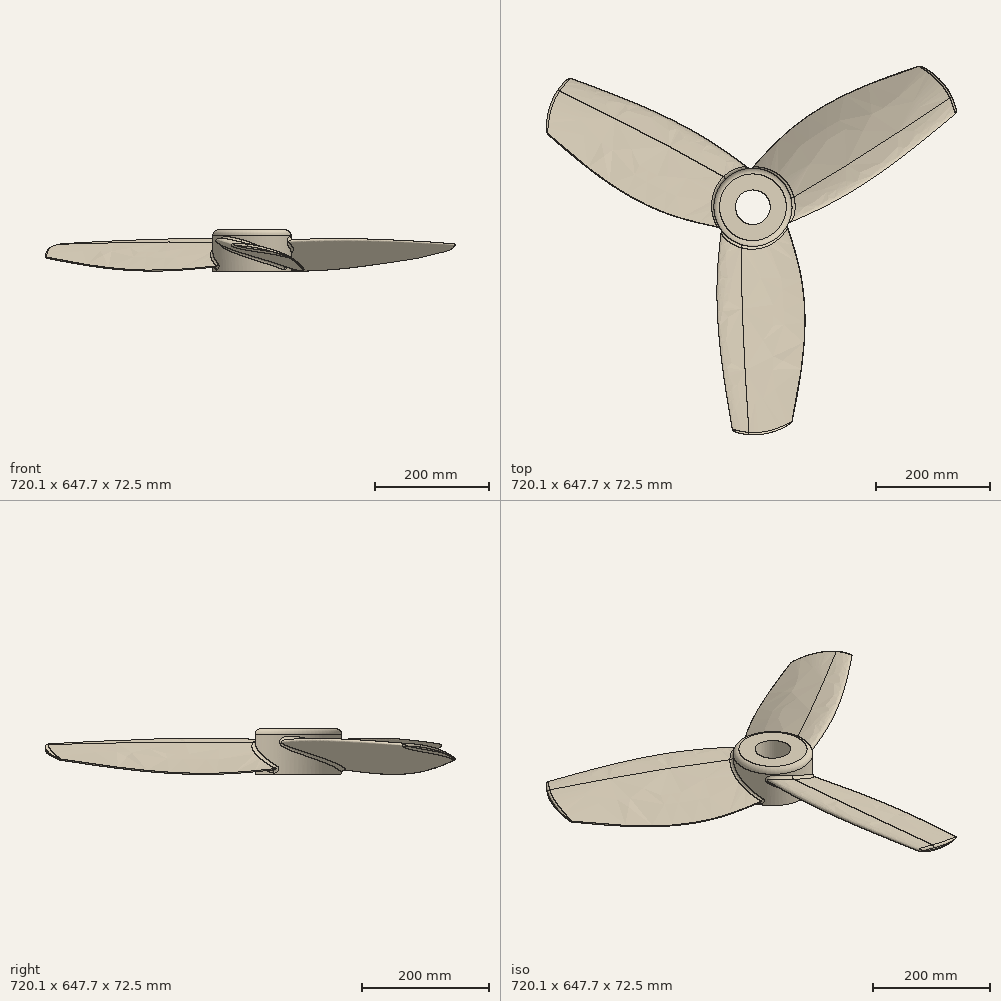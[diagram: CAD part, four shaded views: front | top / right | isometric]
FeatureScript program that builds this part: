
annotation { "Feature Type Name" : "Feature", "Feature Type Description" : "" }
export const myFeature = defineFeature(function(context is Context, id is Id, definition is map)
    precondition{}
    {
        {
            var Q0;
            Q0=qCreatedBy(makeId("Front.planeOp"),FACE);
            var sketch = newSketch(context, id + "F0", { "sketchPlane" : qUnion([Q0])});
            skLineSegment(sketch, "E0", {"start": v(-25.68, 10.16) * mm, "end": v(0, 0) * mm, "construction": true});
            skLineSegment(sketch, "E1", {"start": v(0, 0) * mm, "end": v(25.68, -10.16) * mm, "construction": true});
            skLineSegment(sketch, "E2", {"start": v(25.68, -10.16) * mm, "end": v(51.36, -20.31) * mm, "construction": true});
            skLineSegment(sketch, "E3", {"start": v(51.36, -20.31) * mm, "end": v(77.03, -30.47) * mm, "construction": true});
            skLineSegment(sketch, "E4", {"start": v(0, 0) * mm, "end": v(3.73, 9.44) * mm, "construction": true});
            skLineSegment(sketch, "E5", {"start": v(-25.68, 10.16) * mm, "end": v(-23.81, 14.88) * mm, "construction": true});
            skFitSpline(sketch, "E6", {"points": [v(-25.68, 10.16) * mm, v(3.73, 9.44) * mm, v(77.03, -30.47) * mm], "startDerivative": vector(15.03, 38) * mm, "endDerivative": vector(104.92, -93.69) * mm});
            skPoint(sketch, "E7", {"position": v(1.87, 4.72) * mm});
            skLineSegment(sketch, "E8", {"start": v(-23.81, 14.88) * mm, "end": v(1.87, 4.72) * mm, "construction": true});
            skLineSegment(sketch, "E9", {"start": v(0, 0) * mm, "end": v(-1.87, -4.72) * mm, "construction": true});
            skLineSegment(sketch, "E10", {"start": v(-25.68, 10.16) * mm, "end": v(-27.54, 5.44) * mm, "construction": true});
            skFitSpline(sketch, "E11", {"points": [v(-25.68, 10.16) * mm, v(-1.87, -4.72) * mm, v(77.03, -30.47) * mm], "startDerivative": vector(-15.23, -38.5) * mm, "endDerivative": vector(121.84, -48.19) * mm});
            skLineSegment(sketch, "E12", {"start": v(51.36, -20.31) * mm, "end": v(55.09, -10.87) * mm, "construction": true});
            skSolve(sketch);
        }
        {
            var Q0;
            Q0=qCreatedBy(makeId("Front.planeOp"),FACE);
            cPlane(context, id + "F1", {"entities" : qUnion([Q0]), "cplaneType" : CPlaneType.OFFSET, "offset" : 125 * mm, "width" : 150 * mm, "height" : 150 * mm});
        }
        {
            var Q0;
            Q0=qCreatedBy(id+"F1.planeOp",FACE);
            var sketch = newSketch(context, id + "F2", { "sketchPlane" : qUnion([Q0])});
            skLineSegment(sketch, "E13", {"start": v(-38.33, 14.06) * mm, "end": v(0, 0) * mm, "construction": true});
            skLineSegment(sketch, "E14", {"start": v(0, 0) * mm, "end": v(38.33, -14.06) * mm, "construction": true});
            skLineSegment(sketch, "E15", {"start": v(38.33, -14.06) * mm, "end": v(76.67, -28.12) * mm, "construction": true});
            skLineSegment(sketch, "E16", {"start": v(76.67, -28.12) * mm, "end": v(115, -42.17) * mm, "construction": true});
            skLineSegment(sketch, "E17", {"start": v(0, 0) * mm, "end": v(4.06, 11.06) * mm, "construction": true});
            skLineSegment(sketch, "E18", {"start": v(-38.33, 14.06) * mm, "end": v(-36.3, 19.59) * mm, "construction": true});
            skFitSpline(sketch, "E19", {"points": [v(-38.33, 14.06) * mm, v(4.06, 11.06) * mm, v(115, -42.17) * mm], "startDerivative": vector(16.44, 44.82) * mm, "endDerivative": vector(163.27, -119.63) * mm});
            skPoint(sketch, "E20", {"position": v(2.03, 5.53) * mm});
            skLineSegment(sketch, "E21", {"start": v(-36.3, 19.59) * mm, "end": v(2.03, 5.53) * mm, "construction": true});
            skLineSegment(sketch, "E22", {"start": v(0, 0) * mm, "end": v(-2.03, -5.53) * mm, "construction": true});
            skLineSegment(sketch, "E23", {"start": v(-38.33, 14.06) * mm, "end": v(-40.36, 8.53) * mm, "construction": true});
            skFitSpline(sketch, "E24", {"points": [v(-38.33, 14.06) * mm, v(-2.03, -5.53) * mm, v(115, -42.17) * mm], "startDerivative": vector(-16.57, -45.19) * mm, "endDerivative": vector(181.7, -66.64) * mm});
            skLineSegment(sketch, "E25", {"start": v(76.67, -28.12) * mm, "end": v(80.72, -17.06) * mm, "construction": true});
            skSolve(sketch);
        }
        {
            var Q0;
            Q0=qCreatedBy(makeId("Front.planeOp"),FACE);
            cPlane(context, id + "F3", {"entities" : qUnion([Q0]), "cplaneType" : CPlaneType.OFFSET, "offset" : 400 * mm, "width" : 150 * mm, "height" : 150 * mm});
        }
        {
            var Q0;
            Q0=qCreatedBy(id+"F3.planeOp",FACE);
            var sketch = newSketch(context, id + "F4", { "sketchPlane" : qUnion([Q0])});
            skLineSegment(sketch, "E26", {"start": v(-10.03, 5.14) * mm, "end": v(16.27, 0) * mm, "construction": true});
            skLineSegment(sketch, "E27", {"start": v(16.27, 0) * mm, "end": v(42.56, -5.14) * mm, "construction": true});
            skLineSegment(sketch, "E28", {"start": v(42.56, -5.14) * mm, "end": v(68.86, -10.28) * mm, "construction": true});
            skLineSegment(sketch, "E29", {"start": v(68.86, -10.28) * mm, "end": v(95.16, -15.42) * mm, "construction": true});
            skLineSegment(sketch, "E30", {"start": v(16.27, 0) * mm, "end": v(17.61, 6.9) * mm, "construction": true});
            skLineSegment(sketch, "E31", {"start": v(-10.03, 5.14) * mm, "end": v(-9.36, 8.59) * mm, "construction": true});
            skFitSpline(sketch, "E32", {"points": [v(-10.03, 5.14) * mm, v(17.61, 6.9) * mm, v(95.16, -15.42) * mm], "startDerivative": vector(5.47, 28.01) * mm, "endDerivative": vector(118.7, -57.28) * mm});
            skPoint(sketch, "E33", {"position": v(16.94, 3.45) * mm});
            skLineSegment(sketch, "E34", {"start": v(-9.36, 8.59) * mm, "end": v(16.94, 3.45) * mm, "construction": true});
            skLineSegment(sketch, "E35", {"start": v(16.27, 0) * mm, "end": v(15.6, -3.45) * mm, "construction": true});
            skLineSegment(sketch, "E36", {"start": v(-10.03, 5.14) * mm, "end": v(-10.7, 1.7) * mm, "construction": true});
            skFitSpline(sketch, "E37", {"points": [v(-10.03, 5.14) * mm, v(15.6, -3.45) * mm, v(95.16, -15.42) * mm], "startDerivative": vector(-5.51, -28.2) * mm, "endDerivative": vector(124.61, -24.36) * mm});
            skLineSegment(sketch, "E38", {"start": v(68.86, -10.28) * mm, "end": v(70.2, -3.38) * mm, "construction": true});
            skSolve(sketch);
        }
        {
            var Q0;
            Q0=qSketchRegion(id+"F0",true);
            var Q1;
            Q1=qSketchRegion(id+"F2",true);
            var Q2;
            Q2=qSketchRegion(id+"F4",true);
            var Q3;
            Q3=sQuery(id+"F0.wireOp",VERTEX,"E6.1.internal");
            var Q4;
            Q4=sQuery(id+"F2.wireOp",VERTEX,"E19.1.internal");
            var Q5;
            Q5=sQuery(id+"F4.wireOp",VERTEX,"E30.end");
            loft(context, id + "F5", {"sheetProfilesArray" : [{ "sheetProfileEntities" : qUnion([Q0]) }, { "sheetProfileEntities" : qUnion([Q1]) }, { "sheetProfileEntities" : qUnion([Q2]) }], "matchConnections" : true, "connections" : [{ "connectionEntities" : qUnion([Q3, Q4, Q5]), "connectionEdgeQueries" : qUnion([]), "connectionEdgeParameters" : [] }]});
        }
        {
            var Q0;
            Q0=qCreatedBy(makeId("Top.planeOp"),FACE);
            var sketch = newSketch(context, id + "F6", { "sketchPlane" : qUnion([Q0])});
            skFitSpline(sketch, "E39", {"points": [v(-55.98, -360.47) * mm, v(39.38, -398.87) * mm, v(142.8, -333.19) * mm], "startDerivative": vector(111.22, -150.8) * mm, "endDerivative": vector(54.24, 145.78) * mm});
            skLineSegment(sketch, "E40", {"start": v(-55.98, -360.47) * mm, "end": v(-55.98, -458.75) * mm});
            skLineSegment(sketch, "E41", {"start": v(142.8, -333.19) * mm, "end": v(142.8, -458.75) * mm});
            skLineSegment(sketch, "E42", {"start": v(142.8, -458.75) * mm, "end": v(-55.98, -458.75) * mm});
            skSolve(sketch);
        }
        {
            var Q0;
            Q0=qSketchRegion(id+"F6",true);
            extrude(context, id + "F7", {"entities" : qUnion([Q0]), "operationType" : NewBodyOperationType.REMOVE, "endBound" : BoundingType.SYMMETRIC, "oppositeDirection" : true, "depth" : 40.17 * mm});
        }
        {
            var Q0;
            Q0=makeQuery(id+"F5.opLoft","SWEPT_EDGE",EDGE,{"disambiguationData":[OSD([sQuery(id+"F2.wireOp",EDGE,"E19"),sQuery(id+"F2.wireOp",EDGE,"E24"),sQuery(id+"F4.wireOp",EDGE,"E32"),sQuery(id+"F4.wireOp",EDGE,"E37")])]});
            fillet(context, id + "F8", {"entities" : qUnion([Q0]), "radius" : 1 * mm, "tangentPropagation" : true, "allowEdgeOverflow" : false});
        }
        {
            var Q0;
            Q0=makeQuery(id+"F7.boolean.opBoolean","COPY",FACE,{"derivedFrom":makeQuery(id+"F7.opExtrude","SWEPT_FACE",FACE,{"disambiguationData":[OSD([sQuery(id+"F6.wireOp",EDGE,"E39")])]})});
            fillet(context, id + "F9", {"entities" : qUnion([Q0]), "radius" : 4 * mm, "tangentPropagation" : true, "allowEdgeOverflow" : false});
        }
        {
            var Q0;
            Q0=qCreatedBy(makeId("Top.planeOp"),FACE);
            var sketch = newSketch(context, id + "F10", { "sketchPlane" : qUnion([Q0])});
            skCircle(sketch, "E43", {"center": v(24.35, 0) * mm, "radius": 68.6 * mm});
            skSolve(sketch);
        }
        {
            var Q0;
            Q0=qSketchRegion(id+"F10",true);
            extrude(context, id + "F11", {"entities" : qUnion([Q0]), "depth" : 32.31 * mm, "hasSecondDirection" : true, "secondDirectionOppositeDirection" : true, "secondDirectionDepth" : 40 * mm});
        }
        {
            var Q0;
            Q0=makeQuery(id+"F5.opLoft","SWEPT_BODY",BODY,{"disambiguationData":[OSD([makeQuery(id+"F0.imprint","IMPRINT",FACE,{"disambiguationData":[TD([[makeQuery(id+"F0.imprint","IMPRINT",EDGE,{"derivedFrom":sQuery(id+"F0.wireOp",EDGE,"E6")}),-1.0]])]}),sQuery(id+"F2.wireOp",EDGE,"E24"),makeQuery(id+"F4.imprint","IMPRINT",FACE,{"disambiguationData":[TD([[makeQuery(id+"F4.imprint","IMPRINT",EDGE,{"derivedFrom":sQuery(id+"F4.wireOp",EDGE,"E32")}),-1.0]])]})])]});
            var Q1;
            Q1=makeQuery(id+"F11.opExtrude","SWEPT_FACE",FACE,{"disambiguationData":[OSD([sQuery(id+"F10.wireOp",EDGE,"E43")])]});
            circularPattern(context, id + "F12", {"entities" : qUnion([Q0]), "axis" : qUnion([Q1]), "angle" : 360 * degree, "instanceCount" : round(3), "equalSpace" : true});
        }
        {
            var Q0;
            Q0=makeQuery(id+"F12.opPattern","COPY",BODY,{"derivedFrom":makeQuery(id+"F5.opLoft","SWEPT_BODY",BODY,{"disambiguationData":[OSD([makeQuery(id+"F0.imprint","IMPRINT",FACE,{"disambiguationData":[TD([[makeQuery(id+"F0.imprint","IMPRINT",EDGE,{"derivedFrom":sQuery(id+"F0.wireOp",EDGE,"E6")}),-1.0]])]}),sQuery(id+"F2.wireOp",EDGE,"E24"),makeQuery(id+"F4.imprint","IMPRINT",FACE,{"disambiguationData":[TD([[makeQuery(id+"F4.imprint","IMPRINT",EDGE,{"derivedFrom":sQuery(id+"F4.wireOp",EDGE,"E32")}),-1.0]])]})])]}),"instanceName":"2"});
            var Q1;
            Q1=makeQuery(id+"F5.opLoft","SWEPT_BODY",BODY,{"disambiguationData":[OSD([makeQuery(id+"F0.imprint","IMPRINT",FACE,{"disambiguationData":[TD([[makeQuery(id+"F0.imprint","IMPRINT",EDGE,{"derivedFrom":sQuery(id+"F0.wireOp",EDGE,"E6")}),-1.0]])]}),sQuery(id+"F2.wireOp",EDGE,"E24"),makeQuery(id+"F4.imprint","IMPRINT",FACE,{"disambiguationData":[TD([[makeQuery(id+"F4.imprint","IMPRINT",EDGE,{"derivedFrom":sQuery(id+"F4.wireOp",EDGE,"E32")}),-1.0]])]})])]});
            var Q2;
            Q2=makeQuery(id+"F11.opExtrude","SWEPT_BODY",BODY,{"disambiguationData":[OSD([sQuery(id+"F10.wireOp",EDGE,"E43")])]});
            var Q3;
            Q3=makeQuery(id+"F12.opPattern","COPY",BODY,{"derivedFrom":makeQuery(id+"F5.opLoft","SWEPT_BODY",BODY,{"disambiguationData":[OSD([makeQuery(id+"F0.imprint","IMPRINT",FACE,{"disambiguationData":[TD([[makeQuery(id+"F0.imprint","IMPRINT",EDGE,{"derivedFrom":sQuery(id+"F0.wireOp",EDGE,"E6")}),-1.0]])]}),sQuery(id+"F2.wireOp",EDGE,"E24"),makeQuery(id+"F4.imprint","IMPRINT",FACE,{"disambiguationData":[TD([[makeQuery(id+"F4.imprint","IMPRINT",EDGE,{"derivedFrom":sQuery(id+"F4.wireOp",EDGE,"E32")}),-1.0]])]})])]}),"instanceName":"1"});
            var Q4;
            Q4=makeQuery(id+"F12.opPattern","COPY",BODY,{"derivedFrom":makeQuery(id+"F5.opLoft","SWEPT_BODY",BODY,{"disambiguationData":[OSD([makeQuery(id+"F0.imprint","IMPRINT",FACE,{"disambiguationData":[TD([[makeQuery(id+"F0.imprint","IMPRINT",EDGE,{"derivedFrom":sQuery(id+"F0.wireOp",EDGE,"E6")}),-1.0]])]}),sQuery(id+"F2.wireOp",EDGE,"E24"),makeQuery(id+"F4.imprint","IMPRINT",FACE,{"disambiguationData":[TD([[makeQuery(id+"F4.imprint","IMPRINT",EDGE,{"derivedFrom":sQuery(id+"F4.wireOp",EDGE,"E32")}),-1.0]])]})])]}),"instanceName":"4"});
            var Q5;
            Q5=makeQuery(id+"F12.opPattern","COPY",BODY,{"derivedFrom":makeQuery(id+"F5.opLoft","SWEPT_BODY",BODY,{"disambiguationData":[OSD([makeQuery(id+"F0.imprint","IMPRINT",FACE,{"disambiguationData":[TD([[makeQuery(id+"F0.imprint","IMPRINT",EDGE,{"derivedFrom":sQuery(id+"F0.wireOp",EDGE,"E6")}),-1.0]])]}),sQuery(id+"F2.wireOp",EDGE,"E24"),makeQuery(id+"F4.imprint","IMPRINT",FACE,{"disambiguationData":[TD([[makeQuery(id+"F4.imprint","IMPRINT",EDGE,{"derivedFrom":sQuery(id+"F4.wireOp",EDGE,"E32")}),-1.0]])]})])]}),"instanceName":"3"});
            booleanBodies(context, id + "F13", {"operationType" : BooleanOperationType.UNION, "tools" : qUnion([Q0, Q1, Q2, Q3, Q4, Q5])});
        }
        {
            var Q0;
            Q0=makeQuery(id+"F11.opExtrude","CAP_FACE",FACE,{"disambiguationData":[OSD([sQuery(id+"F10.wireOp",EDGE,"E43")])],"isStart":false});
            var sketch = newSketch(context, id + "F14", { "sketchPlane" : qUnion([Q0])});
            skCircle(sketch, "E44", {"center": v(24.35, 0) * mm, "radius": 30.45 * mm});
            skSolve(sketch);
        }
        {
            var Q0;
            Q0=qSketchRegion(id+"F14",true);
            extrude(context, id + "F15", {"entities" : qUnion([Q0]), "operationType" : NewBodyOperationType.REMOVE, "endBound" : BoundingType.THROUGH_ALL, "oppositeDirection" : true, "depth" : 25 * mm});
        }
        {
            var Q0;
            {var subQ0=sQuery(id+"F0.wireOp",VERTEX,"E6.1.internal");var subQ1=sQuery(id+"F0.wireOp",EDGE,"E6");var subQ2=sQuery(id+"F0.wireOp",EDGE,"E11");var subQ3=sQuery(id+"F2.wireOp",VERTEX,"E19.1.internal");var subQ4=sQuery(id+"F2.wireOp",EDGE,"E19");var subQ5=sQuery(id+"F2.wireOp",EDGE,"E24");Q0=makeQuery(id+"F13.opBoolean","INTERSECT",EDGE,{"derivedFrom":[makeQuery(id+"F11.opExtrude","SWEPT_FACE",FACE,{"disambiguationData":[OSD([sQuery(id+"F10.wireOp",EDGE,"E43")])]}),makeQuery(id+"F12.opPattern","COPY",FACE,{"derivedFrom":makeQuery(id+"F5.opLoft","SWEPT_FACE",FACE,{"disambiguationData":[OSD([subQ0,subQ1,subQ2,subQ3,subQ4,subQ5]),TDD([subQ0,makeQuery(id+"F0.imprint","INTERSECT",VERTEX,{"disambiguationData":[OD(0.0)],"derivedFrom":[subQ1,subQ2]}),makeQuery(id+"F0.imprint","IMPRINT",EDGE,{"derivedFrom":subQ1}),subQ3,makeQuery(id+"F2.imprint","INTERSECT",VERTEX,{"disambiguationData":[OD(0.0)],"derivedFrom":[subQ4,subQ5]}),makeQuery(id+"F2.imprint","IMPRINT",EDGE,{"derivedFrom":subQ4})])]}),"instanceName":"2"})]});}
            var Q1;
            {var subQ0=sQuery(id+"F0.wireOp",VERTEX,"E6.1.internal");var subQ1=sQuery(id+"F0.wireOp",EDGE,"E6");var subQ2=sQuery(id+"F0.wireOp",EDGE,"E11");var subQ3=sQuery(id+"F2.wireOp",VERTEX,"E19.1.internal");var subQ4=sQuery(id+"F2.wireOp",EDGE,"E19");var subQ5=sQuery(id+"F2.wireOp",EDGE,"E24");Q1=makeQuery(id+"F13.opBoolean","INTERSECT",EDGE,{"derivedFrom":[makeQuery(id+"F5.opLoft","SWEPT_FACE",FACE,{"disambiguationData":[OSD([subQ0,subQ1,subQ2,subQ3,subQ4,subQ5]),TDD([subQ0,makeQuery(id+"F0.imprint","INTERSECT",VERTEX,{"disambiguationData":[OD(1.0)],"derivedFrom":[subQ1,subQ2]}),makeQuery(id+"F0.imprint","IMPRINT",EDGE,{"derivedFrom":subQ1}),subQ3,makeQuery(id+"F2.imprint","INTERSECT",VERTEX,{"disambiguationData":[OD(1.0)],"derivedFrom":[subQ4,subQ5]}),makeQuery(id+"F2.imprint","IMPRINT",EDGE,{"derivedFrom":subQ4})])]}),makeQuery(id+"F11.opExtrude","SWEPT_FACE",FACE,{"disambiguationData":[OSD([sQuery(id+"F10.wireOp",EDGE,"E43")])]})]});}
            var Q2;
            {var subQ0=sQuery(id+"F0.wireOp",VERTEX,"E6.1.internal");var subQ1=sQuery(id+"F0.wireOp",EDGE,"E6");var subQ2=sQuery(id+"F0.wireOp",EDGE,"E11");var subQ3=sQuery(id+"F2.wireOp",VERTEX,"E19.1.internal");var subQ4=sQuery(id+"F2.wireOp",EDGE,"E19");var subQ5=sQuery(id+"F2.wireOp",EDGE,"E24");Q2=makeQuery(id+"F13.opBoolean","INTERSECT",EDGE,{"derivedFrom":[makeQuery(id+"F11.opExtrude","SWEPT_FACE",FACE,{"disambiguationData":[OSD([sQuery(id+"F10.wireOp",EDGE,"E43")])]}),makeQuery(id+"F12.opPattern","COPY",FACE,{"derivedFrom":makeQuery(id+"F5.opLoft","SWEPT_FACE",FACE,{"disambiguationData":[OSD([subQ0,subQ1,subQ2,subQ3,subQ4,subQ5]),TDD([subQ0,makeQuery(id+"F0.imprint","INTERSECT",VERTEX,{"disambiguationData":[OD(1.0)],"derivedFrom":[subQ1,subQ2]}),makeQuery(id+"F0.imprint","IMPRINT",EDGE,{"derivedFrom":subQ1}),subQ3,makeQuery(id+"F2.imprint","INTERSECT",VERTEX,{"disambiguationData":[OD(1.0)],"derivedFrom":[subQ4,subQ5]}),makeQuery(id+"F2.imprint","IMPRINT",EDGE,{"derivedFrom":subQ4})])]}),"instanceName":"1"})]});}
            var Q3;
            {var subQ0=sQuery(id+"F0.wireOp",VERTEX,"E6.1.internal");var subQ1=sQuery(id+"F0.wireOp",EDGE,"E6");var subQ2=sQuery(id+"F0.wireOp",EDGE,"E11");var subQ3=sQuery(id+"F2.wireOp",VERTEX,"E19.1.internal");var subQ4=sQuery(id+"F2.wireOp",EDGE,"E19");var subQ5=sQuery(id+"F2.wireOp",EDGE,"E24");Q3=makeQuery(id+"F13.opBoolean","INTERSECT",EDGE,{"derivedFrom":[makeQuery(id+"F11.opExtrude","SWEPT_FACE",FACE,{"disambiguationData":[OSD([sQuery(id+"F10.wireOp",EDGE,"E43")])]}),makeQuery(id+"F12.opPattern","COPY",FACE,{"derivedFrom":makeQuery(id+"F5.opLoft","SWEPT_FACE",FACE,{"disambiguationData":[OSD([subQ0,subQ1,subQ2,subQ3,subQ4,subQ5]),TDD([subQ0,makeQuery(id+"F0.imprint","INTERSECT",VERTEX,{"disambiguationData":[OD(1.0)],"derivedFrom":[subQ1,subQ2]}),makeQuery(id+"F0.imprint","IMPRINT",EDGE,{"derivedFrom":subQ1}),subQ3,makeQuery(id+"F2.imprint","INTERSECT",VERTEX,{"disambiguationData":[OD(1.0)],"derivedFrom":[subQ4,subQ5]}),makeQuery(id+"F2.imprint","IMPRINT",EDGE,{"derivedFrom":subQ4})])]}),"instanceName":"4"})]});}
            var Q4;
            {var subQ0=sQuery(id+"F0.wireOp",VERTEX,"E6.1.internal");var subQ1=sQuery(id+"F0.wireOp",EDGE,"E6");var subQ2=sQuery(id+"F0.wireOp",EDGE,"E11");var subQ3=sQuery(id+"F2.wireOp",VERTEX,"E19.1.internal");var subQ4=sQuery(id+"F2.wireOp",EDGE,"E19");var subQ5=sQuery(id+"F2.wireOp",EDGE,"E24");Q4=makeQuery(id+"F13.opBoolean","INTERSECT",EDGE,{"derivedFrom":[makeQuery(id+"F11.opExtrude","SWEPT_FACE",FACE,{"disambiguationData":[OSD([sQuery(id+"F10.wireOp",EDGE,"E43")])]}),makeQuery(id+"F12.opPattern","COPY",FACE,{"derivedFrom":makeQuery(id+"F5.opLoft","SWEPT_FACE",FACE,{"disambiguationData":[OSD([subQ0,subQ1,subQ2,subQ3,subQ4,subQ5]),TDD([subQ0,makeQuery(id+"F0.imprint","INTERSECT",VERTEX,{"disambiguationData":[OD(0.0)],"derivedFrom":[subQ1,subQ2]}),makeQuery(id+"F0.imprint","IMPRINT",EDGE,{"derivedFrom":subQ1}),subQ3,makeQuery(id+"F2.imprint","INTERSECT",VERTEX,{"disambiguationData":[OD(0.0)],"derivedFrom":[subQ4,subQ5]}),makeQuery(id+"F2.imprint","IMPRINT",EDGE,{"derivedFrom":subQ4})])]}),"instanceName":"3"})]});}
            fillet(context, id + "F16", {"entities" : qUnion([Q0, Q1, Q2, Q3, Q4]), "radius" : 5 * mm, "tangentPropagation" : true, "allowEdgeOverflow" : false});
        }
        {
            var Q0;
            Q0=makeQuery(id+"F11.opExtrude","CAP_EDGE",EDGE,{"disambiguationData":[OSD([sQuery(id+"F10.wireOp",EDGE,"E43")])],"isStart":false});
            fillet(context, id + "F17", {"entities" : qUnion([Q0]), "radius" : 10 * mm, "tangentPropagation" : true, "allowEdgeOverflow" : false});
        }
    });
